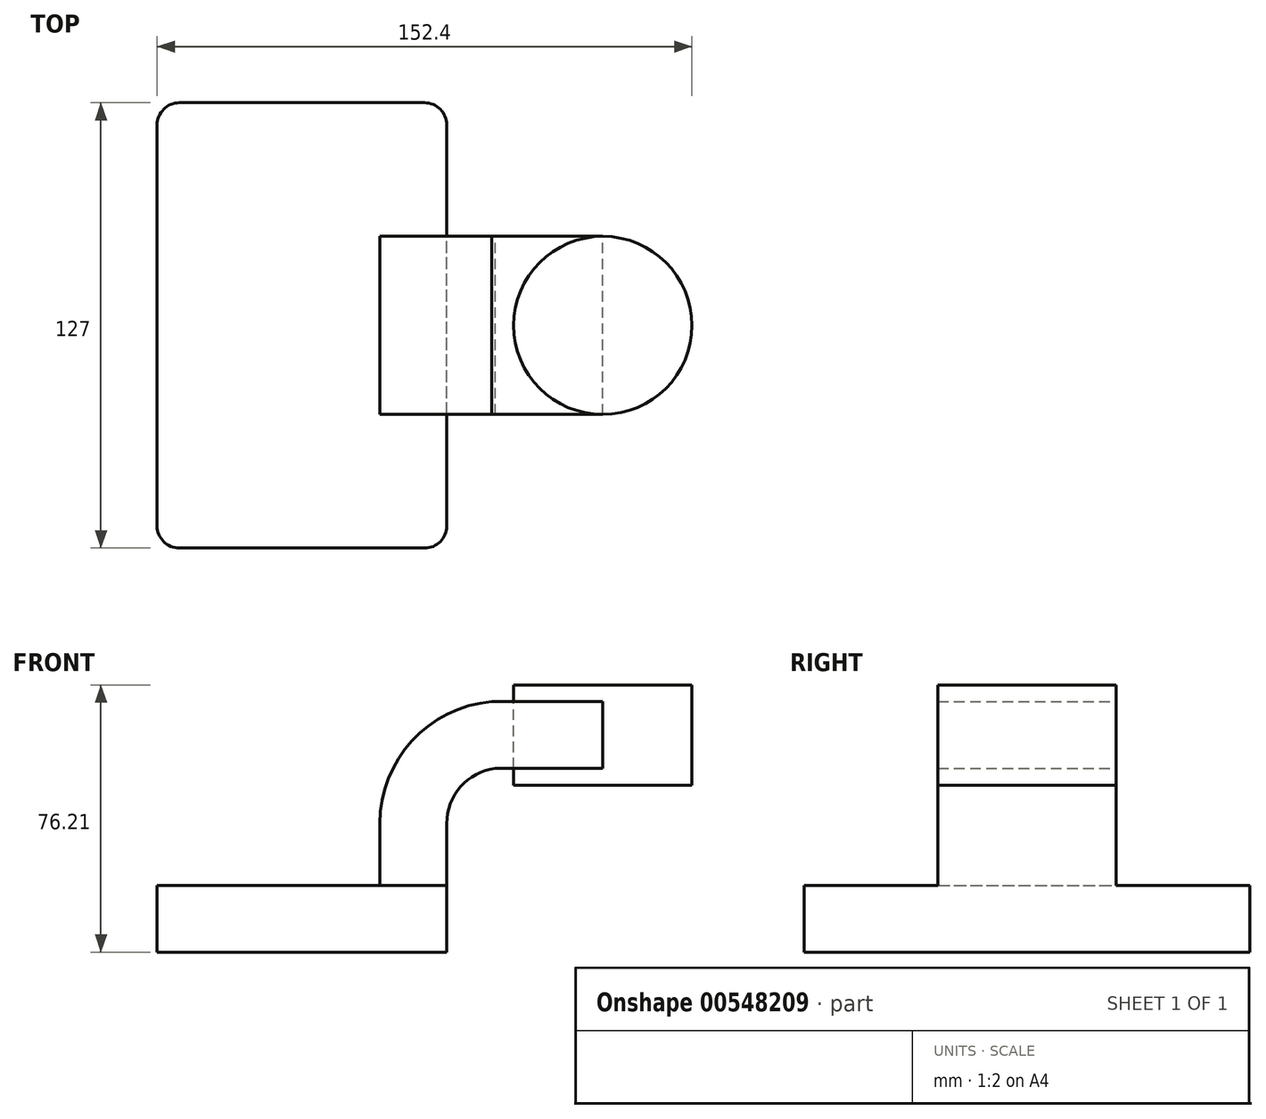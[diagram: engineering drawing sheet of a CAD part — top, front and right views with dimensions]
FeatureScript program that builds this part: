
annotation { "Feature Type Name" : "Feature", "Feature Type Description" : "" }
export const myFeature = defineFeature(function(context is Context, id is Id, definition is map)
    precondition{}
    {
        {
            var Q0;
            Q0=qCreatedBy(makeId("Front.planeOp"),FACE);
            var sketch = newSketch(context, id + "F0", { "sketchPlane" : qUnion([Q0])});
            skLineSegment(sketch, "E0.bottom", {"start": v(-41.28, 9.52) * mm, "end": v(41.27, 9.53) * mm});
            skLineSegment(sketch, "E0.top", {"start": v(-41.28, -9.53) * mm, "end": v(41.28, -9.53) * mm});
            skLineSegment(sketch, "E0.left", {"start": v(-41.28, 9.52) * mm, "end": v(-41.27, -9.53) * mm});
            skLineSegment(sketch, "E0.right", {"start": v(41.28, 9.53) * mm, "end": v(41.28, -9.52) * mm});
            skPoint(sketch, "E0.middle", {"position": v(0, 0) * mm});
            skLineSegment(sketch, "E1.bottom", {"start": v(60.33, 66.68) * mm, "end": v(111.12, 66.68) * mm});
            skLineSegment(sketch, "E1.left", {"start": v(60.33, 66.68) * mm, "end": v(60.33, 38.1) * mm});
            skLineSegment(sketch, "E1.right", {"start": v(111.12, 66.68) * mm, "end": v(111.13, 38.1) * mm});
            skPoint(sketch, "E1.middle", {"position": v(85.73, 52.39) * mm});
            skLineSegment(sketch, "E2", {"start": v(41.27, 9.53) * mm, "end": v(41.27, 27.13) * mm});
            skArc(sketch, "E3", {"start": v(41.27, 27.13) * mm, "mid": v(45.22, 37.6) * mm, "end": v(55.1, 42.88) * mm});
            skLineSegment(sketch, "E4.0", {"start": v(54.1, 61.93) * mm, "end": v(85.73, 61.93) * mm});
            skArc(sketch, "E4.1", {"start": v(22.22, 27.13) * mm, "mid": v(31.4, 50.73) * mm, "end": v(54.1, 61.93) * mm});
            skLineSegment(sketch, "E4.2", {"start": v(22.22, 9.53) * mm, "end": v(22.22, 27.13) * mm});
            skFitSpline(sketch, "E5", {"points": [v(-41.28, 9.53) * mm, v(54.1, 61.93) * mm], "startDerivative": vector(0.78, 96.5) * mm, "endDerivative": vector(96.67, 0) * mm});
            skPoint(sketch, "E6.endSnap0", {"position": v(85.73, 66.68) * mm});
            skLineSegment(sketch, "E7", {"start": v(85.73, 66.68) * mm, "end": v(85.73, 38.1) * mm});
            skLineSegment(sketch, "E8", {"start": v(60.33, 38.1) * mm, "end": v(111.13, 38.1) * mm});
            skLineSegment(sketch, "E9", {"start": v(55.1, 42.88) * mm, "end": v(85.73, 42.88) * mm});
            skSolve(sketch);
        }
        {
            var Q0;
            Q0=makeQuery(id+"F0.imprint","IMPRINT",FACE,{"disambiguationData":[TD([[makeQuery(id+"F0.imprint","IMPRINT",EDGE,{"derivedFrom":sQuery(id+"F0.wireOp",EDGE,"E0.top")}),1.0]])]});
            extrude(context, id + "F1", {"entities" : qUnion([Q0]), "endBound" : BoundingType.SYMMETRIC, "depth" : 127 * mm, "offsetDistance" : 25.4 * mm});
        }
        {
            var Q0;
            {var subQ1=sQuery(id+"F0.wireOp",EDGE,"E2");Q0=makeQuery(id+"F0.imprint","IMPRINT",FACE,{"disambiguationData":[TD([[makeQuery(id+"F0.imprint","IMPRINT",EDGE,{"derivedFrom":subQ1}),1.0]])]});}
            var Q1;
            {var subQ0=sQuery(id+"F0.wireOp",EDGE,"E4.0");var subQ1=sQuery(id+"F0.wireOp",EDGE,"E1.left");var subQ2=makeQuery(id+"F0.imprint","INTERSECT",VERTEX,{"derivedFrom":[subQ1,subQ0]});Q1=makeQuery(id+"F0.imprint","IMPRINT",FACE,{"disambiguationData":[TD([[makeQuery(id+"F0.imprint","IMPRINT",EDGE,{"disambiguationData":[TD([[subQ2,-1.0]])],"derivedFrom":subQ1}),1.0]])]});}
            extrude(context, id + "F2", {"entities" : qUnion([Q0, Q1]), "operationType" : NewBodyOperationType.ADD, "endBound" : BoundingType.SYMMETRIC, "depth" : 50.8 * mm, "offsetDistance" : 25.4 * mm});
        }
        {
            var Q0;
            Q0=makeQuery(id+"F0.imprint","IMPRINT",FACE,{"disambiguationData":[TD([[makeQuery(id+"F0.imprint","IMPRINT",EDGE,{"derivedFrom":sQuery(id+"F0.wireOp",EDGE,"E4.1")}),1.0]])]});
            extrude(context, id + "F3", {"entities" : qUnion([Q0]), "operationType" : NewBodyOperationType.ADD, "endBound" : BoundingType.SYMMETRIC, "depth" : 15.88 * mm, "offsetDistance" : 25.4 * mm});
        }
        {
            var Q0;
            {var subQ5=sQuery(id+"F0.wireOp",EDGE,"E1.right");Q0=makeQuery(id+"F0.imprint","IMPRINT",FACE,{"disambiguationData":[TD([[makeQuery(id+"F0.imprint","IMPRINT",EDGE,{"derivedFrom":subQ5}),-1.0]])]});}
            var Q1;
            Q1=sQuery(id+"F0.wireOp",EDGE,"E7");
            revolve(context, id + "F4", {"entities" : qUnion([Q0]), "axis" : qUnion([Q1]), "revolveType" : RevolveType.FULL});
        }
        {
            var Q0;
            Q0=makeQuery(id+"F1.opExtrude","CAP_EDGE",EDGE,{"disambiguationData":[OSD([sQuery(id+"F0.wireOp",EDGE,"E0.right")])],"isStart":false});
            var Q1;
            Q1=makeQuery(id+"F1.opExtrude","CAP_EDGE",EDGE,{"disambiguationData":[OSD([sQuery(id+"F0.wireOp",EDGE,"E0.right")])],"isStart":true});
            var Q2;
            Q2=makeQuery(id+"F1.opExtrude","CAP_EDGE",EDGE,{"disambiguationData":[OSD([sQuery(id+"F0.wireOp",EDGE,"E0.left")])],"isStart":true});
            var Q3;
            Q3=makeQuery(id+"F1.opExtrude","CAP_EDGE",EDGE,{"disambiguationData":[OSD([sQuery(id+"F0.wireOp",EDGE,"E0.left")])],"isStart":false});
            fillet(context, id + "F5", {"entities" : qUnion([Q0, Q1, Q2, Q3]), "radius" : 6.35 * mm, "tangentPropagation" : true, "allowEdgeOverflow" : false});
        }
    });
